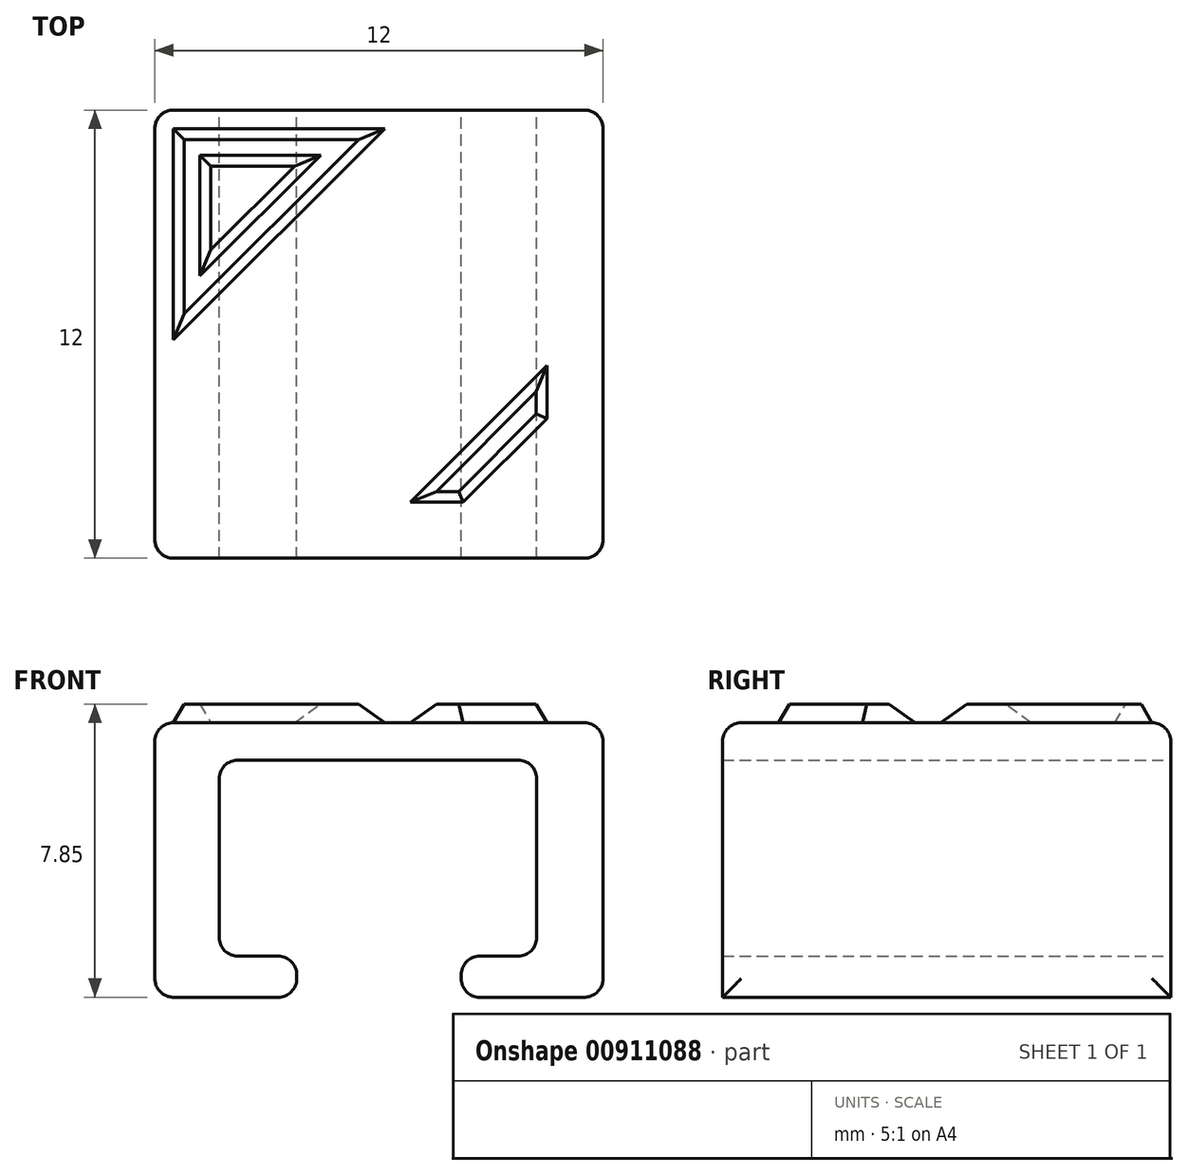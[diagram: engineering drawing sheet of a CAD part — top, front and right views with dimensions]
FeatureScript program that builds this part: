
annotation { "Feature Type Name" : "Feature", "Feature Type Description" : "" }
export const myFeature = defineFeature(function(context is Context, id is Id, definition is map)
    precondition{}
    {
        {
            var Q0;
            Q0=qCreatedBy(makeId("Front.planeOp"),FACE);
            var sketch = newSketch(context, id + "F0", { "sketchPlane" : qUnion([Q0])});
            skLineSegment(sketch, "E0.bottom", {"start": v(6, 2.8) * mm, "end": v(-6, 2.8) * mm});
            skLineSegment(sketch, "E0.top", {"start": v(6, -4.55) * mm, "end": v(-6, -4.55) * mm});
            skLineSegment(sketch, "E0.left", {"start": v(6, 2.8) * mm, "end": v(6, -4.55) * mm});
            skLineSegment(sketch, "E0.right", {"start": v(-6, 2.8) * mm, "end": v(-6, -4.55) * mm});
            skPoint(sketch, "E0.middle", {"position": v(0, -0.88) * mm});
            skLineSegment(sketch, "E1.0", {"start": v(4.23, -3.45) * mm, "end": v(-4.27, -3.45) * mm});
            skLineSegment(sketch, "E2", {"start": v(0, -3.45) * mm, "end": v(0, -4.55) * mm});
            skLineSegment(sketch, "E3.0", {"start": v(-2.2, -3.35) * mm, "end": v(-2.2, -4.55) * mm});
            skLineSegment(sketch, "E4.MirrorCS", {"start": v(2.2, -3.35) * mm, "end": v(2.2, -4.55) * mm});
            skLineSegment(sketch, "E5.0", {"start": v(-4.28, 1.8) * mm, "end": v(-4.27, -3.45) * mm});
            skLineSegment(sketch, "E6.0", {"start": v(4.23, 1.8) * mm, "end": v(4.23, -3.45) * mm});
            skLineSegment(sketch, "E7.0", {"start": v(4.23, 1.8) * mm, "end": v(-4.28, 1.8) * mm});
            skPoint(sketch, "E8.orphan", {"position": v(6.17, -3.45) * mm});
            skPoint(sketch, "E9.orphan", {"position": v(-6.17, -3.45) * mm});
            skLineSegment(sketch, "E10", {"start": v(0, 2.8) * mm, "end": v(-0.02, 1.8) * mm, "construction": true});
            skSolve(sketch);
        }
        {
            var Q0;
            Q0=makeQuery(id+"F0.imprint","IMPRINT",FACE,{"disambiguationData":[TD([[makeQuery(id+"F0.imprint","IMPRINT",EDGE,{"derivedFrom":sQuery(id+"F0.wireOp",EDGE,"E0.bottom")}),1.0]])]});
            extrude(context, id + "F1", {"entities" : qUnion([Q0]), "depth" : 12 * mm, "symmetric" : true});
        }
        {
            var Q0;
            Q0=makeQuery(id+"F1.opExtrude","SWEPT_EDGE",EDGE,{"disambiguationData":[OSD([sQuery(id+"F0.wireOp",EDGE,"E0.top"),sQuery(id+"F0.wireOp",EDGE,"E3.0")])]});
            var Q1;
            Q1=makeQuery(id+"F1.opExtrude","SWEPT_EDGE",EDGE,{"disambiguationData":[OSD([sQuery(id+"F0.wireOp",EDGE,"E0.top"),sQuery(id+"F0.wireOp",EDGE,"E4.MirrorCS")])]});
            var Q2;
            Q2=makeQuery(id+"F1.opExtrude","SWEPT_EDGE",EDGE,{"disambiguationData":[OSD([sQuery(id+"F0.wireOp",EDGE,"E1.0"),sQuery(id+"F0.wireOp",EDGE,"E3.0")])]});
            var Q3;
            Q3=makeQuery(id+"F1.opExtrude","SWEPT_EDGE",EDGE,{"disambiguationData":[OSD([sQuery(id+"F0.wireOp",EDGE,"E1.0"),sQuery(id+"F0.wireOp",EDGE,"E4.MirrorCS")])]});
            fillet(context, id + "F2", {"entities" : qUnion([Q0, Q1, Q2, Q3]), "radius" : .5 * mm, "tangentPropagation" : true, "allowEdgeOverflow" : false});
        }
        {
            var Q0;
            Q0=makeQuery(id+"F1.opExtrude","SWEPT_FACE",FACE,{"disambiguationData":[OSD([sQuery(id+"F0.wireOp",EDGE,"E0.left")])]});
            var Q1;
            Q1=makeQuery(id+"F1.opExtrude","SWEPT_FACE",FACE,{"disambiguationData":[OSD([sQuery(id+"F0.wireOp",EDGE,"E0.bottom")])]});
            var Q2;
            Q2=makeQuery(id+"F1.opExtrude","SWEPT_FACE",FACE,{"disambiguationData":[OSD([sQuery(id+"F0.wireOp",EDGE,"E0.right")])]});
            fillet(context, id + "F3", {"entities" : qUnion([Q0, Q1, Q2]), "radius" : .5 * mm, "tangentPropagation" : true, "allowEdgeOverflow" : false});
        }
        {
            var Q0;
            Q0=makeQuery(id+"F1.opExtrude","SWEPT_FACE",FACE,{"disambiguationData":[OSD([sQuery(id+"F0.wireOp",EDGE,"E0.bottom")])]});
            var sketch = newSketch(context, id + "F4", { "sketchPlane" : qUnion([Q0])});
            skLineSegment(sketch, "E11.0.0", {"start": v(5.5, -5.5) * mm, "end": v(5.5, 5.5) * mm});
            skLineSegment(sketch, "E11.0.1", {"start": v(5.5, 5.5) * mm, "end": v(-5.5, 5.5) * mm});
            skLineSegment(sketch, "E11.0.2", {"start": v(-5.5, 5.5) * mm, "end": v(-5.5, -5.5) * mm});
            skLineSegment(sketch, "E11.0.3", {"start": v(-5.5, -5.5) * mm, "end": v(5.5, -5.5) * mm});
            skLineSegment(sketch, "E12", {"start": v(0.16, 5.5) * mm, "end": v(-5.5, -0.16) * mm});
            skLineSegment(sketch, "E13", {"start": v(5.5, 0.16) * mm, "end": v(-0.16, -5.5) * mm});
            skLineSegment(sketch, "E14.0", {"start": v(-4.5, -4.5) * mm, "end": v(4.5, -4.5) * mm});
            skLineSegment(sketch, "E14.1", {"start": v(-4.5, 4.5) * mm, "end": v(-4.5, -4.5) * mm});
            skLineSegment(sketch, "E14.2", {"start": v(4.5, 4.5) * mm, "end": v(-4.5, 4.5) * mm});
            skLineSegment(sketch, "E14.3", {"start": v(4.5, -4.5) * mm, "end": v(4.5, 4.5) * mm});
            skLineSegment(sketch, "E15.0", {"start": v(10.5, -5.5) * mm, "end": v(10.5, 5.5) * mm});
            skLineSegment(sketch, "E16.0", {"start": v(4.5, -2.26) * mm, "end": v(2.26, -4.5) * mm});
            skLineSegment(sketch, "E17.0", {"start": v(10.5, -10.5) * mm, "end": v(10.5, 10.5) * mm});
            skLineSegment(sketch, "E17.1", {"start": v(-10.5, -10.5) * mm, "end": v(10.5, -10.5) * mm});
            skLineSegment(sketch, "E17.2", {"start": v(-10.5, 10.5) * mm, "end": v(-10.5, -10.5) * mm});
            skLineSegment(sketch, "E17.3", {"start": v(10.5, 10.5) * mm, "end": v(-10.5, 10.5) * mm});
            skLineSegment(sketch, "E18.0", {"start": v(-0.3, 6.46) * mm, "end": v(-5.96, 0.8) * mm});
            skSolve(sketch);
        }
        {
            var Q0;
            {var subQ3=sQuery(id+"F4.wireOp",EDGE,"E12");Q0=makeQuery(id+"F4.imprint","IMPRINT",FACE,{"disambiguationData":[TD([[makeQuery(id+"F4.imprint","IMPRINT",EDGE,{"derivedFrom":subQ3}),-1.0]])]});}
            var Q1;
            {var subQ3=sQuery(id+"F4.wireOp",EDGE,"E13");Q1=makeQuery(id+"F4.imprint","IMPRINT",FACE,{"disambiguationData":[TD([[makeQuery(id+"F4.imprint","IMPRINT",EDGE,{"derivedFrom":subQ3}),1.0]])]});}
            var Q2;
            {var subQ5=sQuery(id+"F4.wireOp",EDGE,"E11.0.2");var subQ8=sQuery(id+"F4.wireOp",EDGE,"E11.0.1");var subQ9=makeQuery(id+"F4.imprint","INTERSECT",VERTEX,{"derivedFrom":[subQ8,subQ5]});Q2=makeQuery(id+"F4.imprint","IMPRINT",FACE,{"disambiguationData":[TD([[makeQuery(id+"F4.imprint","IMPRINT",EDGE,{"disambiguationData":[TD([[subQ9,1.0]])],"derivedFrom":subQ8}),1.0]])]});}
            var Q3;
            {var subQ5=sQuery(id+"F4.wireOp",EDGE,"E16.0");Q3=makeQuery(id+"F4.imprint","IMPRINT",FACE,{"disambiguationData":[TD([[makeQuery(id+"F4.imprint","IMPRINT",EDGE,{"derivedFrom":subQ5}),-1.0]])]});}
            extrude(context, id + "F5", {"entities" : qUnion([Q0, Q1, Q2, Q3]), "operationType" : NewBodyOperationType.ADD, "depth" : .5 * mm, "offsetDistance" : 25 * mm, "hasDraft" : true, "draftAngle" : 30 * degree, "draftPullDirection" : true});
        }
        {
            var Q0;
            Q0=makeQuery(id+"F1.opExtrude","SWEPT_EDGE",EDGE,{"disambiguationData":[OSD([sQuery(id+"F0.wireOp",EDGE,"E5.0"),sQuery(id+"F0.wireOp",EDGE,"E7.0")])]});
            var Q1;
            Q1=makeQuery(id+"F1.opExtrude","SWEPT_EDGE",EDGE,{"disambiguationData":[OSD([sQuery(id+"F0.wireOp",EDGE,"E6.0"),sQuery(id+"F0.wireOp",EDGE,"E7.0")])]});
            var Q2;
            Q2=makeQuery(id+"F1.opExtrude","SWEPT_EDGE",EDGE,{"disambiguationData":[OSD([sQuery(id+"F0.wireOp",EDGE,"E1.0"),sQuery(id+"F0.wireOp",EDGE,"E5.0")])]});
            var Q3;
            Q3=makeQuery(id+"F1.opExtrude","SWEPT_EDGE",EDGE,{"disambiguationData":[OSD([sQuery(id+"F0.wireOp",EDGE,"E1.0"),sQuery(id+"F0.wireOp",EDGE,"E6.0")])]});
            fillet(context, id + "F6", {"entities" : qUnion([Q0, Q1, Q2, Q3]), "radius" : .5 * mm, "tangentPropagation" : true, "allowEdgeOverflow" : false});
        }
    });
